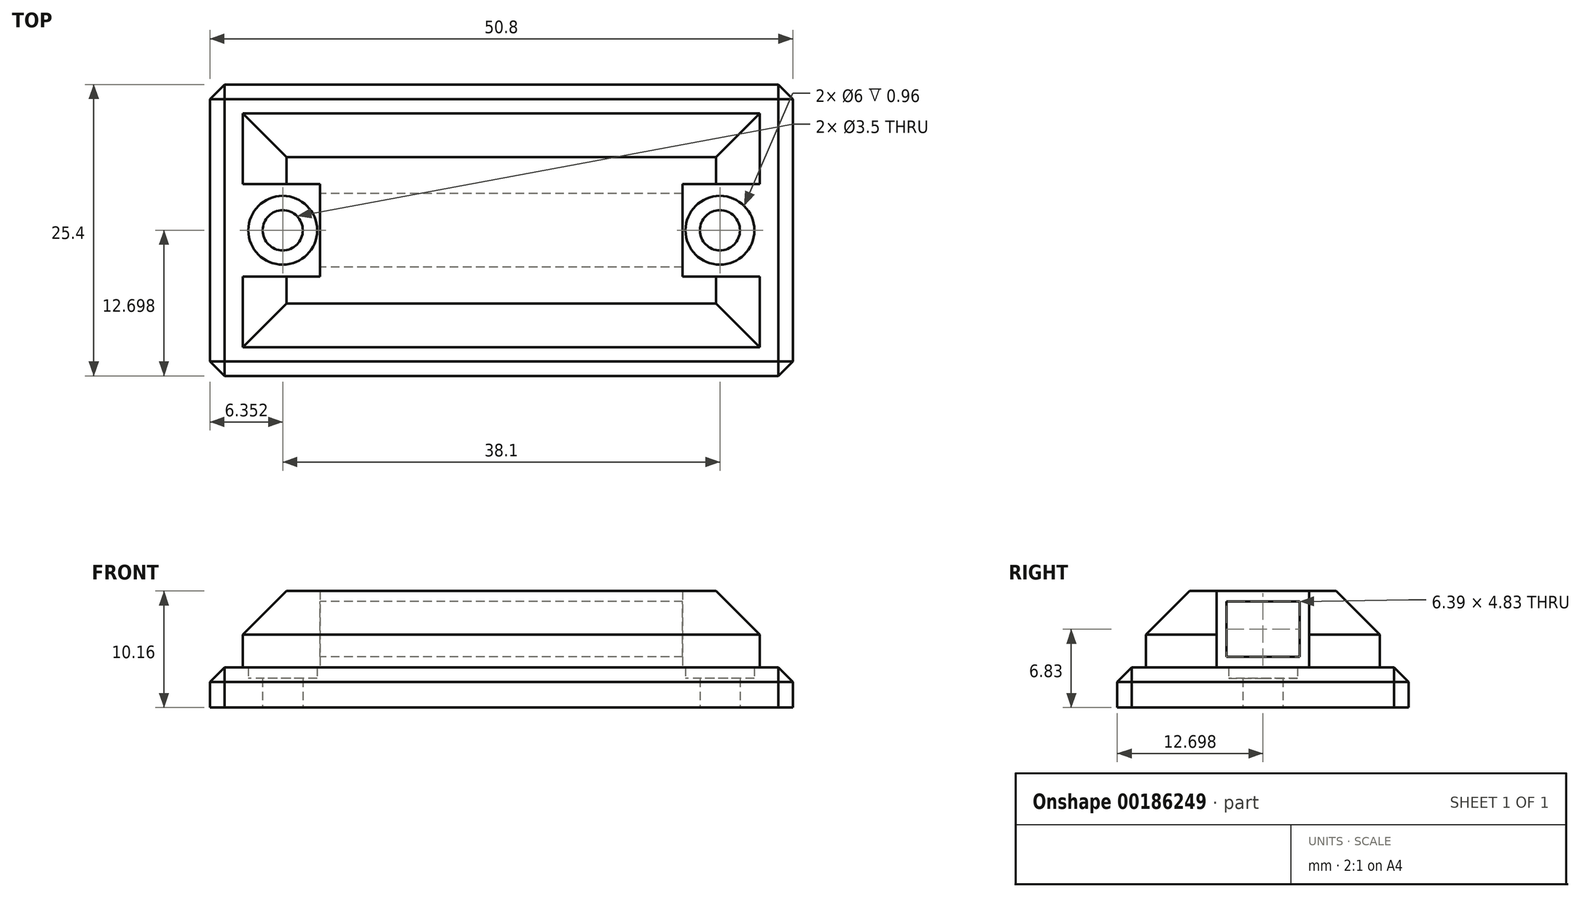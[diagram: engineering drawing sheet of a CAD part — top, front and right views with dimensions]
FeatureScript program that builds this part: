
annotation { "Feature Type Name" : "Feature", "Feature Type Description" : "" }
export const myFeature = defineFeature(function(context is Context, id is Id, definition is map)
    precondition{}
    {
        {
            var Q0;
            Q0=qCreatedBy(makeId("Top.planeOp"),FACE);
            var sketch = newSketch(context, id + "F0", { "sketchPlane" : qUnion([Q0])});
            skLineSegment(sketch, "E0.bottom", {"start": v(-22.7, 47.06) * mm, "end": v(28.1, 47.06) * mm});
            skLineSegment(sketch, "E0.top", {"start": v(-22.7, 21.66) * mm, "end": v(28.1, 21.66) * mm});
            skLineSegment(sketch, "E0.left", {"start": v(-22.7, 47.06) * mm, "end": v(-22.7, 21.66) * mm});
            skLineSegment(sketch, "E0.right", {"start": v(28.1, 47.06) * mm, "end": v(28.1, 21.66) * mm});
            skPoint(sketch, "E0.middle", {"position": v(2.7, 34.36) * mm});
            skCircle(sketch, "E1", {"center": v(-16.35, 34.36) * mm, "radius": 1.75 * mm});
            skCircle(sketch, "E2", {"center": v(21.75, 34.36) * mm, "radius": 1.75 * mm});
            skLineSegment(sketch, "E3", {"start": v(21.75, 34.36) * mm, "end": v(-16.35, 34.36) * mm, "construction": true});
            skLineSegment(sketch, "E4.bottom", {"start": v(-19.83, 44.55) * mm, "end": v(25.23, 44.55) * mm});
            skLineSegment(sketch, "E4.top", {"start": v(-19.83, 24.17) * mm, "end": v(25.23, 24.17) * mm});
            skLineSegment(sketch, "E4.left", {"start": v(-19.83, 44.55) * mm, "end": v(-19.83, 38.4) * mm});
            skLineSegment(sketch, "E4.right", {"start": v(25.23, 44.55) * mm, "end": v(25.23, 38.4) * mm});
            skLineSegment(sketch, "E5", {"start": v(-19.83, 38.4) * mm, "end": v(-13.1, 38.4) * mm});
            skLineSegment(sketch, "E6", {"start": v(-13.1, 38.4) * mm, "end": v(-13.1, 30.32) * mm});
            skLineSegment(sketch, "E7", {"start": v(2.7, 44.55) * mm, "end": v(2.7, 24.7) * mm, "construction": true});
            skLineSegment(sketch, "E8.MirrorCS", {"start": v(-28.9, 44.55) * mm, "end": v(-28.9, 24.7) * mm, "construction": true});
            skLineSegment(sketch, "E9.MirrorCS", {"start": v(18.5, 38.4) * mm, "end": v(18.5, 30.32) * mm});
            skLineSegment(sketch, "E10.MirrorCS", {"start": v(-19.83, 30.32) * mm, "end": v(-13.1, 30.32) * mm});
            skLineSegment(sketch, "E11.trimOffspring", {"start": v(-19.83, 30.32) * mm, "end": v(-19.83, 24.17) * mm});
            skLineSegment(sketch, "E12.trimOffspring", {"start": v(25.23, 30.32) * mm, "end": v(25.23, 24.17) * mm});
            skLineSegment(sketch, "E13.trimOffspring", {"start": v(18.5, 38.4) * mm, "end": v(25.23, 38.4) * mm});
            skPoint(sketch, "E14.orphan", {"position": v(-13.1, 44.55) * mm});
            skPoint(sketch, "E15.orphan", {"position": v(-13.1, 24.17) * mm});
            skPoint(sketch, "E16.orphan", {"position": v(18.5, 24.17) * mm});
            skPoint(sketch, "E17.orphan", {"position": v(18.5, 44.55) * mm});
            skLineSegment(sketch, "E18.trimOffspring", {"start": v(18.5, 30.32) * mm, "end": v(25.23, 30.32) * mm});
            skCircle(sketch, "E19", {"center": v(21.75, 34.36) * mm, "radius": 3 * mm});
            skCircle(sketch, "E20", {"center": v(-16.35, 34.36) * mm, "radius": 3 * mm});
            skSolve(sketch);
        }
        {
            var Q0;
            Q0=makeQuery(id+"F0.imprint","IMPRINT",FACE,{"disambiguationData":[TD([[makeQuery(id+"F0.imprint","IMPRINT",EDGE,{"derivedFrom":sQuery(id+"F0.wireOp",EDGE,"E0.bottom")}),-1.0]])]});
            extrude(context, id + "F1", {"entities" : qUnion([Q0]), "depth" : 3.5 * mm});
        }
        {
            var Q0;
            Q0=makeQuery(id+"F0.imprint","IMPRINT",FACE,{"disambiguationData":[TD([[makeQuery(id+"F0.imprint","IMPRINT",EDGE,{"derivedFrom":sQuery(id+"F0.wireOp",EDGE,"E4.bottom")}),-1.0]])]});
            extrude(context, id + "F2", {"entities" : qUnion([Q0]), "operationType" : NewBodyOperationType.ADD, "depth" : 10.16 * mm});
        }
        {
            var Q0;
            Q0=makeQuery(id+"F1.opExtrude","CAP_EDGE",EDGE,{"disambiguationData":[OSD([sQuery(id+"F0.wireOp",EDGE,"E0.left")])],"isStart":false});
            var Q1;
            Q1=makeQuery(id+"F1.opExtrude","CAP_EDGE",EDGE,{"disambiguationData":[OSD([sQuery(id+"F0.wireOp",EDGE,"E0.top")])],"isStart":false});
            var Q2;
            Q2=makeQuery(id+"F1.opExtrude","CAP_EDGE",EDGE,{"disambiguationData":[OSD([sQuery(id+"F0.wireOp",EDGE,"E0.bottom")])],"isStart":false});
            var Q3;
            Q3=makeQuery(id+"F1.opExtrude","CAP_EDGE",EDGE,{"disambiguationData":[OSD([sQuery(id+"F0.wireOp",EDGE,"E0.right")])],"isStart":false});
            var Q4;
            Q4=makeQuery(id+"F1.opExtrude","SWEPT_EDGE",EDGE,{"disambiguationData":[OSD([sQuery(id+"F0.wireOp",EDGE,"E0.bottom"),sQuery(id+"F0.wireOp",EDGE,"E0.left")])]});
            var Q5;
            Q5=makeQuery(id+"F1.opExtrude","SWEPT_EDGE",EDGE,{"disambiguationData":[OSD([sQuery(id+"F0.wireOp",EDGE,"E0.top"),sQuery(id+"F0.wireOp",EDGE,"E0.left")])]});
            var Q6;
            Q6=makeQuery(id+"F1.opExtrude","SWEPT_EDGE",EDGE,{"disambiguationData":[OSD([sQuery(id+"F0.wireOp",EDGE,"E0.top"),sQuery(id+"F0.wireOp",EDGE,"E0.right")])]});
            var Q7;
            Q7=makeQuery(id+"F1.opExtrude","SWEPT_EDGE",EDGE,{"disambiguationData":[OSD([sQuery(id+"F0.wireOp",EDGE,"E0.bottom"),sQuery(id+"F0.wireOp",EDGE,"E0.right")])]});
            chamfer(context, id + "F3", {"entities" : qUnion([Q0, Q1, Q2, Q3, Q4, Q5, Q6, Q7]), "width" : 1.27 * mm, "tangentPropagation" : true});
        }
        {
            var Q0;
            Q0=makeQuery(id+"F2.opExtrude","CAP_EDGE",EDGE,{"disambiguationData":[OSD([sQuery(id+"F0.wireOp",EDGE,"E4.right")])],"isStart":false});
            var Q1;
            Q1=makeQuery(id+"F2.opExtrude","CAP_EDGE",EDGE,{"disambiguationData":[OSD([sQuery(id+"F0.wireOp",EDGE,"E4.bottom")])],"isStart":false});
            var Q2;
            Q2=makeQuery(id+"F2.opExtrude","CAP_EDGE",EDGE,{"disambiguationData":[OSD([sQuery(id+"F0.wireOp",EDGE,"E12.trimOffspring")])],"isStart":false});
            var Q3;
            Q3=makeQuery(id+"F2.opExtrude","CAP_EDGE",EDGE,{"disambiguationData":[OSD([sQuery(id+"F0.wireOp",EDGE,"E4.top")])],"isStart":false});
            var Q4;
            Q4=makeQuery(id+"F2.opExtrude","CAP_EDGE",EDGE,{"disambiguationData":[OSD([sQuery(id+"F0.wireOp",EDGE,"E4.left")])],"isStart":false});
            var Q5;
            Q5=makeQuery(id+"F2.opExtrude","CAP_EDGE",EDGE,{"disambiguationData":[OSD([sQuery(id+"F0.wireOp",EDGE,"E11.trimOffspring")])],"isStart":false});
            chamfer(context, id + "F4", {"entities" : qUnion([Q0, Q1, Q2, Q3, Q4, Q5]), "width" : 3.8 * mm, "tangentPropagation" : true});
        }
        {
            var Q0;
            Q0=makeQuery(id+"F0.imprint","IMPRINT",FACE,{"disambiguationData":[TD([[makeQuery(id+"F0.imprint","IMPRINT",EDGE,{"derivedFrom":sQuery(id+"F0.wireOp",EDGE,"E2")}),-1.0]])]});
            var Q1;
            Q1=makeQuery(id+"F0.imprint","IMPRINT",FACE,{"disambiguationData":[TD([[makeQuery(id+"F0.imprint","IMPRINT",EDGE,{"derivedFrom":sQuery(id+"F0.wireOp",EDGE,"E1")}),-1.0]])]});
            extrude(context, id + "F5", {"entities" : qUnion([Q0, Q1]), "operationType" : NewBodyOperationType.ADD, "depth" : 2.54 * mm});
        }
        {
            var Q0;
            Q0=makeQuery(id+"F2.opExtrude","SWEPT_FACE",FACE,{"disambiguationData":[OSD([sQuery(id+"F0.wireOp",EDGE,"E6")])]});
            var sketch = newSketch(context, id + "F6", { "sketchPlane" : qUnion([Q0])});
            skLineSegment(sketch, "E21.bottom", {"start": v(-31.16, 4.41) * mm, "end": v(-37.55, 4.41) * mm});
            skLineSegment(sketch, "E21.top", {"start": v(-31.16, 9.25) * mm, "end": v(-37.55, 9.25) * mm});
            skLineSegment(sketch, "E21.left", {"start": v(-31.16, 4.41) * mm, "end": v(-31.16, 9.25) * mm});
            skLineSegment(sketch, "E21.right", {"start": v(-37.55, 4.41) * mm, "end": v(-37.55, 9.25) * mm});
            skPoint(sketch, "E21.middle", {"position": v(-34.36, 6.83) * mm});
            skPoint(sketch, "E21.middle.positionSnap0", {"position": v(-38.4, 6.83) * mm});
            skPoint(sketch, "E21.middle.positionSnap1", {"position": v(-34.36, 10.16) * mm});
            skPoint(sketch, "E21.centerSnap0", {"position": v(-38.4, 6.83) * mm});
            skPoint(sketch, "E21.centerSnap1", {"position": v(-34.36, 10.16) * mm});
            skSolve(sketch);
        }
        {
            var Q0;
            Q0 = qSketchRegion(id + "F6", true);
            var Q1;
            Q1=makeQuery(id+"F2.opExtrude","SWEPT_FACE",FACE,{"disambiguationData":[OSD([sQuery(id+"F0.wireOp",EDGE,"E9.MirrorCS")])]});
            extrude(context, id + "F7", {"entities" : qUnion([Q0]), "operationType" : NewBodyOperationType.REMOVE, "endBound" : BoundingType.UP_TO_SURFACE, "oppositeDirection" : true, "endBoundEntityFace" : qUnion([Q1]), "depth" : 25.4 * mm});
        }
    });
